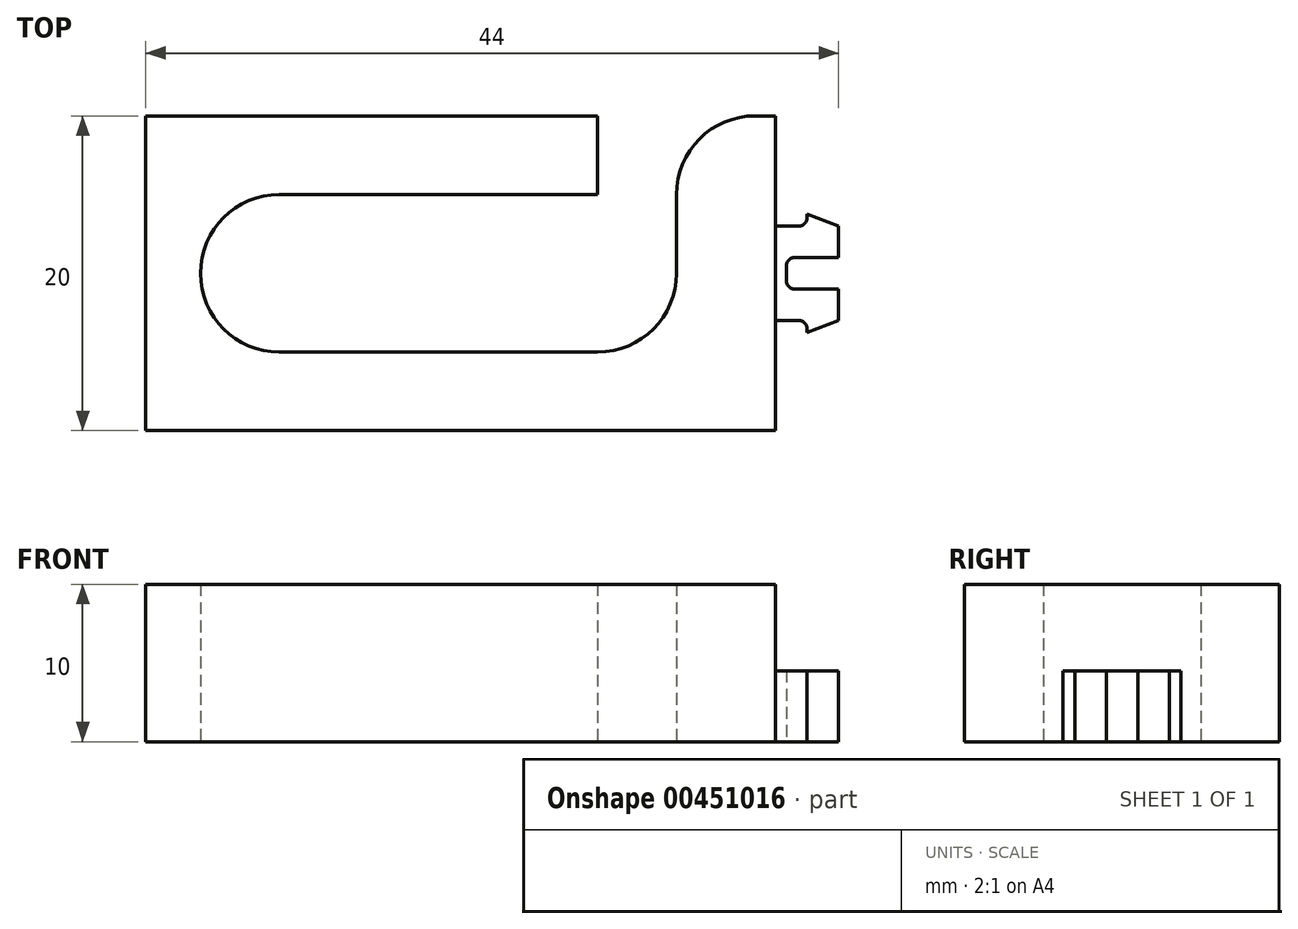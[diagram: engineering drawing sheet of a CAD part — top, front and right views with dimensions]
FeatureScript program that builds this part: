
annotation { "Feature Type Name" : "Feature", "Feature Type Description" : "" }
export const myFeature = defineFeature(function(context is Context, id is Id, definition is map)
    precondition{}
    {
        {
            var Q0;
            Q0=qCreatedBy(makeId("Top.planeOp"),FACE);
            var sketch = newSketch(context, id + "F0", { "sketchPlane" : qUnion([Q0])});
            skLineSegment(sketch, "E0.bottom", {"start": v(-0.94, 0) * mm, "end": v(39.06, 0) * mm});
            skLineSegment(sketch, "E0.top", {"start": v(-0.94, 20) * mm, "end": v(39.06, 20) * mm});
            skLineSegment(sketch, "E0.left", {"start": v(-0.94, 0) * mm, "end": v(-0.94, 20) * mm});
            skLineSegment(sketch, "E0.right", {"start": v(39.06, 0) * mm, "end": v(39.06, 20) * mm});
            skLineSegment(sketch, "E1.bottom", {"start": v(2.54, 15) * mm, "end": v(32.76, 15) * mm});
            skLineSegment(sketch, "E1.top", {"start": v(2.54, 5) * mm, "end": v(32.76, 5) * mm});
            skLineSegment(sketch, "E1.left", {"start": v(2.54, 15) * mm, "end": v(2.54, 5) * mm});
            skLineSegment(sketch, "E1.right", {"start": v(32.76, 15) * mm, "end": v(32.76, 5) * mm});
            skLineSegment(sketch, "E2", {"start": v(5.68, 0) * mm, "end": v(5.68, 5) * mm});
            skLineSegment(sketch, "E3", {"start": v(5.68, 15) * mm, "end": v(5.68, 20) * mm});
            skLineSegment(sketch, "E4.bottom", {"start": v(32.76, 15) * mm, "end": v(27.76, 15) * mm});
            skLineSegment(sketch, "E4.top", {"start": v(32.76, 20) * mm, "end": v(27.76, 20) * mm});
            skLineSegment(sketch, "E4.left", {"start": v(32.76, 15) * mm, "end": v(32.76, 20) * mm});
            skLineSegment(sketch, "E4.right", {"start": v(27.76, 15) * mm, "end": v(27.76, 20) * mm});
            skPoint(sketch, "E5", {"position": v(32.76, 10) * mm});
            skLineSegment(sketch, "E6.bottom", {"start": v(39.06, 13) * mm, "end": v(43.06, 13) * mm});
            skLineSegment(sketch, "E6.top", {"start": v(39.06, 11) * mm, "end": v(43.06, 11) * mm});
            skLineSegment(sketch, "E6.left", {"start": v(39.06, 13) * mm, "end": v(39.06, 11) * mm});
            skLineSegment(sketch, "E6.right", {"start": v(43.06, 13) * mm, "end": v(43.06, 11) * mm});
            skLineSegment(sketch, "E7.bottom", {"start": v(39.06, 7) * mm, "end": v(43.06, 7) * mm});
            skLineSegment(sketch, "E7.top", {"start": v(39.06, 9) * mm, "end": v(43.06, 9) * mm});
            skLineSegment(sketch, "E7.left", {"start": v(39.06, 7) * mm, "end": v(39.06, 9) * mm});
            skLineSegment(sketch, "E7.right", {"start": v(43.06, 7) * mm, "end": v(43.06, 9) * mm});
            skLineSegment(sketch, "E8", {"start": v(43.06, 13) * mm, "end": v(41.06, 13.75) * mm});
            skLineSegment(sketch, "E9", {"start": v(41.06, 13.75) * mm, "end": v(41.06, 6.25) * mm});
            skLineSegment(sketch, "E10", {"start": v(41.06, 6.25) * mm, "end": v(43.06, 7) * mm});
            skPoint(sketch, "E11", {"position": v(41.06, 10) * mm});
            skPoint(sketch, "E12", {"position": v(39.06, 10) * mm});
            skLineSegment(sketch, "E13", {"start": v(39.76, 11) * mm, "end": v(39.76, 9) * mm});
            skSolve(sketch);
        }
        {
            var Q0;
            {var subQ4=sQuery(id+"F0.wireOp",EDGE,"E0.left");Q0=makeQuery(id+"F0.imprint","IMPRINT",FACE,{"disambiguationData":[TD([[makeQuery(id+"F0.imprint","IMPRINT",EDGE,{"derivedFrom":subQ4}),-1.0]])]});}
            var Q1;
            {var subQ9=sQuery(id+"F0.wireOp",EDGE,"E1.right");Q1=makeQuery(id+"F0.imprint","IMPRINT",FACE,{"disambiguationData":[TD([[makeQuery(id+"F0.imprint","IMPRINT",EDGE,{"derivedFrom":subQ9}),1.0]])]});}
            var Q2;
            {var subQ0=sQuery(id+"F0.wireOp",EDGE,"E3");Q2=makeQuery(id+"F0.imprint","IMPRINT",FACE,{"disambiguationData":[TD([[makeQuery(id+"F0.imprint","IMPRINT",EDGE,{"derivedFrom":subQ0}),-1.0]])]});}
            extrude(context, id + "F1", {"entities" : qUnion([Q0, Q1, Q2]), "depth" : 10 * mm});
        }
        {
            var Q0;
            {var subQ0=sQuery(id+"F0.wireOp",EDGE,"E7.top");var subQ1=sQuery(id+"F0.wireOp",EDGE,"E0.right");var subQ2=makeQuery(id+"F0.imprint","INTERSECT",VERTEX,{"derivedFrom":[subQ1,subQ0]});Q0=makeQuery(id+"F0.imprint","IMPRINT",FACE,{"disambiguationData":[TD([[makeQuery(id+"F0.imprint","IMPRINT",EDGE,{"disambiguationData":[TD([[subQ2,1.0]])],"derivedFrom":subQ1}),-1.0]])]});}
            var Q1;
            {var subQ3=sQuery(id+"F0.wireOp",EDGE,"E7.right");Q1=makeQuery(id+"F0.imprint","IMPRINT",FACE,{"disambiguationData":[TD([[makeQuery(id+"F0.imprint","IMPRINT",EDGE,{"derivedFrom":subQ3}),1.0]])]});}
            var Q2;
            {var subQ3=sQuery(id+"F0.wireOp",EDGE,"E10");Q2=makeQuery(id+"F0.imprint","IMPRINT",FACE,{"disambiguationData":[TD([[makeQuery(id+"F0.imprint","IMPRINT",EDGE,{"derivedFrom":subQ3}),1.0]])]});}
            var Q3;
            {var subQ2=sQuery(id+"F0.wireOp",EDGE,"E0.right");var subQ6=sQuery(id+"F0.wireOp",EDGE,"E6.bottom");var subQ8=makeQuery(id+"F0.imprint","INTERSECT",VERTEX,{"derivedFrom":[subQ2,subQ6]});Q3=makeQuery(id+"F0.imprint","IMPRINT",FACE,{"disambiguationData":[TD([[makeQuery(id+"F0.imprint","IMPRINT",EDGE,{"disambiguationData":[TD([[subQ8,1.0]])],"derivedFrom":subQ2}),-1.0]])]});}
            var Q4;
            {var subQ3=sQuery(id+"F0.wireOp",EDGE,"E6.right");Q4=makeQuery(id+"F0.imprint","IMPRINT",FACE,{"disambiguationData":[TD([[makeQuery(id+"F0.imprint","IMPRINT",EDGE,{"derivedFrom":subQ3}),-1.0]])]});}
            var Q5;
            {var subQ3=sQuery(id+"F0.wireOp",EDGE,"E8");Q5=makeQuery(id+"F0.imprint","IMPRINT",FACE,{"disambiguationData":[TD([[makeQuery(id+"F0.imprint","IMPRINT",EDGE,{"derivedFrom":subQ3}),1.0]])]});}
            var Q6;
            {var subQ5=sQuery(id+"F0.wireOp",EDGE,"E13");Q6=makeQuery(id+"F0.imprint","IMPRINT",FACE,{"disambiguationData":[TD([[makeQuery(id+"F0.imprint","IMPRINT",EDGE,{"derivedFrom":subQ5}),-1.0]])]});}
            extrude(context, id + "F2", {"entities" : qUnion([Q0, Q1, Q2, Q3, Q4, Q5, Q6]), "operationType" : NewBodyOperationType.ADD, "depth" : 4.5 * mm});
        }
        {
            var Q0;
            Q0=makeQuery(id+"FwrvMl2xzgpzGwf_1.opExtrude","CAP_EDGE",EDGE,{"disambiguationData":[OSD([sQuery(id+"F4PTOhtl7EFL90g_1.wireOp",EDGE,"oZkCBkvO-QUaH-s3bU-aoQX-DPy4y0Fgcs5u.top")])],"isStart":false});
            var Q1;
            Q1=makeQuery(id+"FwrvMl2xzgpzGwf_1.opExtrude","CAP_EDGE",EDGE,{"disambiguationData":[OSD([sQuery(id+"F4PTOhtl7EFL90g_1.wireOp",EDGE,"oZkCBkvO-QUaH-s3bU-aoQX-DPy4y0Fgcs5u.bottom")])],"isStart":false});
            var Q2;
            Q2=makeQuery(id+"F1.opExtrude","SWEPT_EDGE",EDGE,{"disambiguationData":[OSD([sQuery(id+"F0.wireOp",EDGE,"E1.bottom"),sQuery(id+"F0.wireOp",EDGE,"E1.left")])]});
            var Q3;
            Q3=makeQuery(id+"F1.opExtrude","SWEPT_EDGE",EDGE,{"disambiguationData":[OSD([sQuery(id+"F0.wireOp",EDGE,"E1.top"),sQuery(id+"F0.wireOp",EDGE,"E1.left")])]});
            var Q4;
            Q4=makeQuery(id+"F1.opExtrude","SWEPT_EDGE",EDGE,{"disambiguationData":[OSD([sQuery(id+"F0.wireOp",EDGE,"E1.top"),sQuery(id+"F0.wireOp",EDGE,"E1.right")])]});
            var Q5;
            Q5=makeQuery(id+"F1.opExtrude","SWEPT_EDGE",EDGE,{"disambiguationData":[OSD([sQuery(id+"F0.wireOp",EDGE,"E0.top"),sQuery(id+"F0.wireOp",EDGE,"E4.left")])]});
            fillet(context, id + "F3", {"entities" : qUnion([Q0, Q1, Q2, Q3, Q4, Q5]), "radius" : 5 * mm, "tangentPropagation" : true, "allowEdgeOverflow" : false});
        }
        {
            var Q0;
            Q0=makeQuery(id+"F2.opExtrude","SWEPT_EDGE",EDGE,{"disambiguationData":[OSD([sQuery(id+"F0.wireOp",EDGE,"E0.right"),sQuery(id+"F0.wireOp",EDGE,"E6.bottom")])]});
            var Q1;
            Q1=makeQuery(id+"F2.opExtrude","SWEPT_EDGE",EDGE,{"disambiguationData":[OSD([sQuery(id+"F0.wireOp",EDGE,"E0.right"),sQuery(id+"F0.wireOp",EDGE,"E7.bottom")])]});
            var Q2;
            Q2=makeQuery(id+"F2.opExtrude","SWEPT_EDGE",EDGE,{"disambiguationData":[OSD([sQuery(id+"F0.wireOp",EDGE,"E0.right"),sQuery(id+"F0.wireOp",EDGE,"E6.bottom")])]});
            var Q3;
            Q3=makeQuery(id+"F2.opExtrude","SWEPT_EDGE",EDGE,{"disambiguationData":[OSD([sQuery(id+"F0.wireOp",EDGE,"E0.right"),sQuery(id+"F0.wireOp",EDGE,"E7.bottom")])]});
            var Q4;
            Q4=makeQuery(id+"F2.opExtrude","SWEPT_EDGE",EDGE,{"disambiguationData":[OSD([sQuery(id+"F0.wireOp",EDGE,"E7.bottom"),sQuery(id+"F0.wireOp",EDGE,"E9")])]});
            var Q5;
            Q5=makeQuery(id+"F2.opExtrude","SWEPT_EDGE",EDGE,{"disambiguationData":[OSD([sQuery(id+"F0.wireOp",EDGE,"E6.bottom"),sQuery(id+"F0.wireOp",EDGE,"E9")])]});
            var Q6;
            Q6=makeQuery(id+"F2.opExtrude","SWEPT_EDGE",EDGE,{"disambiguationData":[OSD([sQuery(id+"F0.wireOp",EDGE,"E6.top"),sQuery(id+"F0.wireOp",EDGE,"E13")])]});
            var Q7;
            Q7=makeQuery(id+"F2.opExtrude","SWEPT_EDGE",EDGE,{"disambiguationData":[OSD([sQuery(id+"F0.wireOp",EDGE,"E7.top"),sQuery(id+"F0.wireOp",EDGE,"E13")])]});
            fillet(context, id + "F4", {"entities" : qUnion([Q0, Q1, Q2, Q3, Q4, Q5, Q6, Q7]), "radius" : 0.5 * mm, "tangentPropagation" : true, "allowEdgeOverflow" : false});
        }
    });
